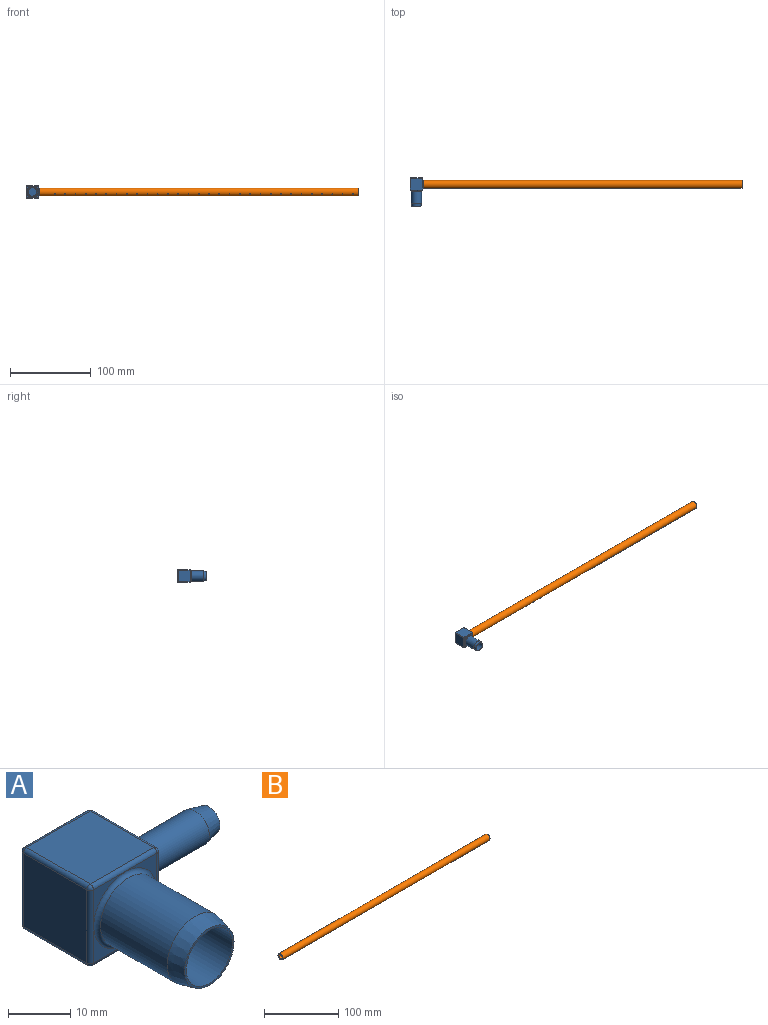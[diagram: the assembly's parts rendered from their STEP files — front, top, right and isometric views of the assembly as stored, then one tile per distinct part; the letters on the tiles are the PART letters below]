
ASSEMBLY  parts=2 mates=1
PART A: 37 faces, bbox 35.3x34.9x16.6 mm
  f0: plane 14.35x14.35mm, normal (0,0,-1), area 206mm2, adj f25,f30,f33,f36
  f1: plane 14.35x14.35mm, normal (1,0,0), area 157.3mm2, adj f15,f22,f31,f32,f36
  f2: plane 14.35x14.35mm, normal (0,0,1), area 206mm2, adj f17,f21,f22,f23
  f3: plane 14.35x14.35mm, normal (-1,0,0), area 206mm2, adj f17,f20,f24,f25
  f4: plane 14.35x14.35mm, normal (0,-1,0), area 47mm2, adj f16,f20,f21,f30,f31
  f5: plane 14.35x14.35mm, normal (0,1,0), area 206mm2, adj f23,f24,f32,f33
  f6: cylinder r=6.35mm len=15.11mm, axis (0,1,0), area 603mm2, adj f14,f16
  f7: plane 11.18x11.18mm, normal (0,-1,0), area 12.9mm2, adj f10,f14
  f8: cylinder r=3.17mm len=15.11mm, axis (-1,0,0), area 301.5mm2, adj f13,f15
  f9: plane 4.83x4.83mm, normal (1,0,0), area 5.3mm2, adj f12,f13
  f10: cylinder r=5.21mm len=30.16mm, axis (0,-1,0), area 973.6mm2, adj f7,f11,f12
  f11: plane 10.41x10.41mm, normal (0,-1,0), area 85.2mm2, adj f10
  f12: cylinder r=2.03mm len=22.19mm, axis (1,0,0), area 280.7mm2, adj f9,f10
  f13: cone r=2.41mm half-angle=13.5deg, axis (-1,0,0), area 57.3mm2, adj f8,f9
  f14: cone r=5.59mm half-angle=13.5deg, axis (0,1,0), area 122.5mm2, adj f6,f7
  f15: torus R=3.94mm, axis (-1,0,0), area 26mm2, adj f1,f8
  f16: torus R=7.11mm, axis (0,-1,0), area 49.8mm2, adj f4,f6
  f17: cylinder r=0.76mm len=14.35mm, axis (0,-1,0), area 17.2mm2, adj f2,f3,f18,f19
  f18: sphere r=0.76mm, area 0.9mm2, adj f17,f20,f21
  f19: sphere r=0.76mm, area 0.9mm2, adj f17,f23,f24
  f20: cylinder r=0.76mm len=14.35mm, axis (0,0,1), area 17.2mm2, adj f3,f4,f18,f26
  f21: cylinder r=0.76mm len=14.35mm, axis (1,0,0), area 17.2mm2, adj f2,f4,f18,f27
  f22: cylinder r=0.76mm len=14.35mm, axis (0,1,0), area 17.2mm2, adj f1,f2,f27,f28
  f23: cylinder r=0.76mm len=14.35mm, axis (-1,0,0), area 17.2mm2, adj f2,f5,f19,f28
  f24: cylinder r=0.76mm len=14.35mm, axis (0,0,-1), area 17.2mm2, adj f3,f5,f19,f29
  f25: cylinder r=0.76mm len=14.35mm, axis (0,1,0), area 17.2mm2, adj f0,f3,f26,f29
  f26: sphere r=0.76mm, area 0.9mm2, adj f20,f25,f30
  f27: sphere r=0.76mm, area 0.9mm2, adj f21,f22,f31
  f28: sphere r=0.76mm, area 0.9mm2, adj f22,f23,f32
  f29: sphere r=0.76mm, area 0.9mm2, adj f24,f25,f33
  f30: cylinder r=0.76mm len=14.35mm, axis (-1,0,0), area 17.2mm2, adj f0,f4,f26,f34
  f31: cylinder r=0.76mm len=14.35mm, axis (0,0,-1), area 17.2mm2, adj f1,f4,f27,f34
  f32: cylinder r=0.76mm len=14.35mm, axis (0,0,1), area 17.2mm2, adj f1,f5,f28,f35
  f33: cylinder r=0.76mm len=14.35mm, axis (1,0,0), area 17.2mm2, adj f0,f5,f29,f35
  f34: sphere r=0.76mm, area 0.9mm2, adj f30,f31,f36
  f35: sphere r=0.76mm, area 0.9mm2, adj f32,f33,f36
  f36: cylinder r=0.76mm len=14.35mm, axis (0,-1,0), area 17.2mm2, adj f0,f1,f34,f35
PART B: 34 faces, bbox 393.7x9.5x9.5 mm
  f0: cylinder r=3.17mm len=393.7mm, axis (-1,0,0), area 7829.6mm2, adj f2,f3,f4,f5,f6,f7,f8,f9
  f1: cylinder r=4.76mm len=393.7mm, axis (-1,0,0), area 11756.6mm2, adj f2,f3,f4,f5,f6,f7,f8,f9
  f2: plane 9.53x9.53mm, normal (1,0,0), area 39.6mm2, adj f0,f1
  f3: plane 9.53x9.53mm, normal (-1,0,0), area 39.6mm2, adj f0,f1
  f4: cylinder r=0.51mm len=1.63mm, axis (0,0,1), area 5.1mm2, adj f0,f1
  f5: cylinder r=0.51mm len=1.63mm, axis (0,0,1), area 5.1mm2, adj f0,f1
  f6: cylinder r=0.51mm len=1.63mm, axis (0,0,1), area 5.1mm2, adj f0,f1
  f7: cylinder r=0.51mm len=1.63mm, axis (0,0,1), area 5.1mm2, adj f0,f1
  f8: cylinder r=0.51mm len=1.63mm, axis (0,0,1), area 5.1mm2, adj f0,f1
  f9: cylinder r=0.51mm len=1.63mm, axis (0,0,1), area 5.1mm2, adj f0,f1
  f10: cylinder r=0.51mm len=1.63mm, axis (0,0,1), area 5.1mm2, adj f0,f1
  f11: cylinder r=0.51mm len=1.63mm, axis (0,0,1), area 5.1mm2, adj f0,f1
  f12: cylinder r=0.51mm len=1.63mm, axis (0,0,1), area 5.1mm2, adj f0,f1
  f13: cylinder r=0.51mm len=1.63mm, axis (0,0,1), area 5.1mm2, adj f0,f1
  f14: cylinder r=0.51mm len=1.63mm, axis (0,0,1), area 5.1mm2, adj f0,f1
  f15: cylinder r=0.51mm len=1.63mm, axis (0,0,1), area 5.1mm2, adj f0,f1
  f16: cylinder r=0.51mm len=1.63mm, axis (0,0,1), area 5.1mm2, adj f0,f1
  f17: cylinder r=0.51mm len=1.63mm, axis (0,0,1), area 5.1mm2, adj f0,f1
  f18: cylinder r=0.51mm len=1.63mm, axis (0,0,1), area 5.1mm2, adj f0,f1
  f19: cylinder r=0.51mm len=1.63mm, axis (0,0,1), area 5.1mm2, adj f0,f1
  f20: cylinder r=0.51mm len=1.63mm, axis (0,0,1), area 5.1mm2, adj f0,f1
  f21: cylinder r=0.51mm len=1.63mm, axis (0,0,1), area 5.1mm2, adj f0,f1
  f22: cylinder r=0.51mm len=1.63mm, axis (0,0,1), area 5.1mm2, adj f0,f1
  f23: cylinder r=0.51mm len=1.63mm, axis (0,0,1), area 5.1mm2, adj f0,f1
  f24: cylinder r=0.51mm len=1.63mm, axis (0,0,1), area 5.1mm2, adj f0,f1
  f25: cylinder r=0.51mm len=1.63mm, axis (0,0,1), area 5.1mm2, adj f0,f1
  f26: cylinder r=0.51mm len=1.63mm, axis (0,0,1), area 5.1mm2, adj f0,f1
  f27: cylinder r=0.51mm len=1.63mm, axis (0,0,1), area 5.1mm2, adj f0,f1
  f28: cylinder r=0.51mm len=1.63mm, axis (0,0,1), area 5.1mm2, adj f0,f1
  f29: cylinder r=0.51mm len=1.63mm, axis (0,0,1), area 5.1mm2, adj f0,f1
  f30: cylinder r=0.51mm len=1.63mm, axis (0,0,1), area 5.1mm2, adj f0,f1
  f31: cylinder r=0.51mm len=1.63mm, axis (0,0,1), area 5.1mm2, adj f0,f1
  f32: cylinder r=0.51mm len=1.63mm, axis (0,0,1), area 5.1mm2, adj f0,f1
  f33: cylinder r=0.51mm len=1.63mm, axis (0,0,1), area 5.1mm2, adj f0,f1
PLACE A at identity fixed
PLACE B rot(axis=(-1,0,0),60deg) t=(205.55,0,0)mm
MATE revolute A.f8 <-> B.f1  axis (-1,0,0) through (8.7,0,0)mm
